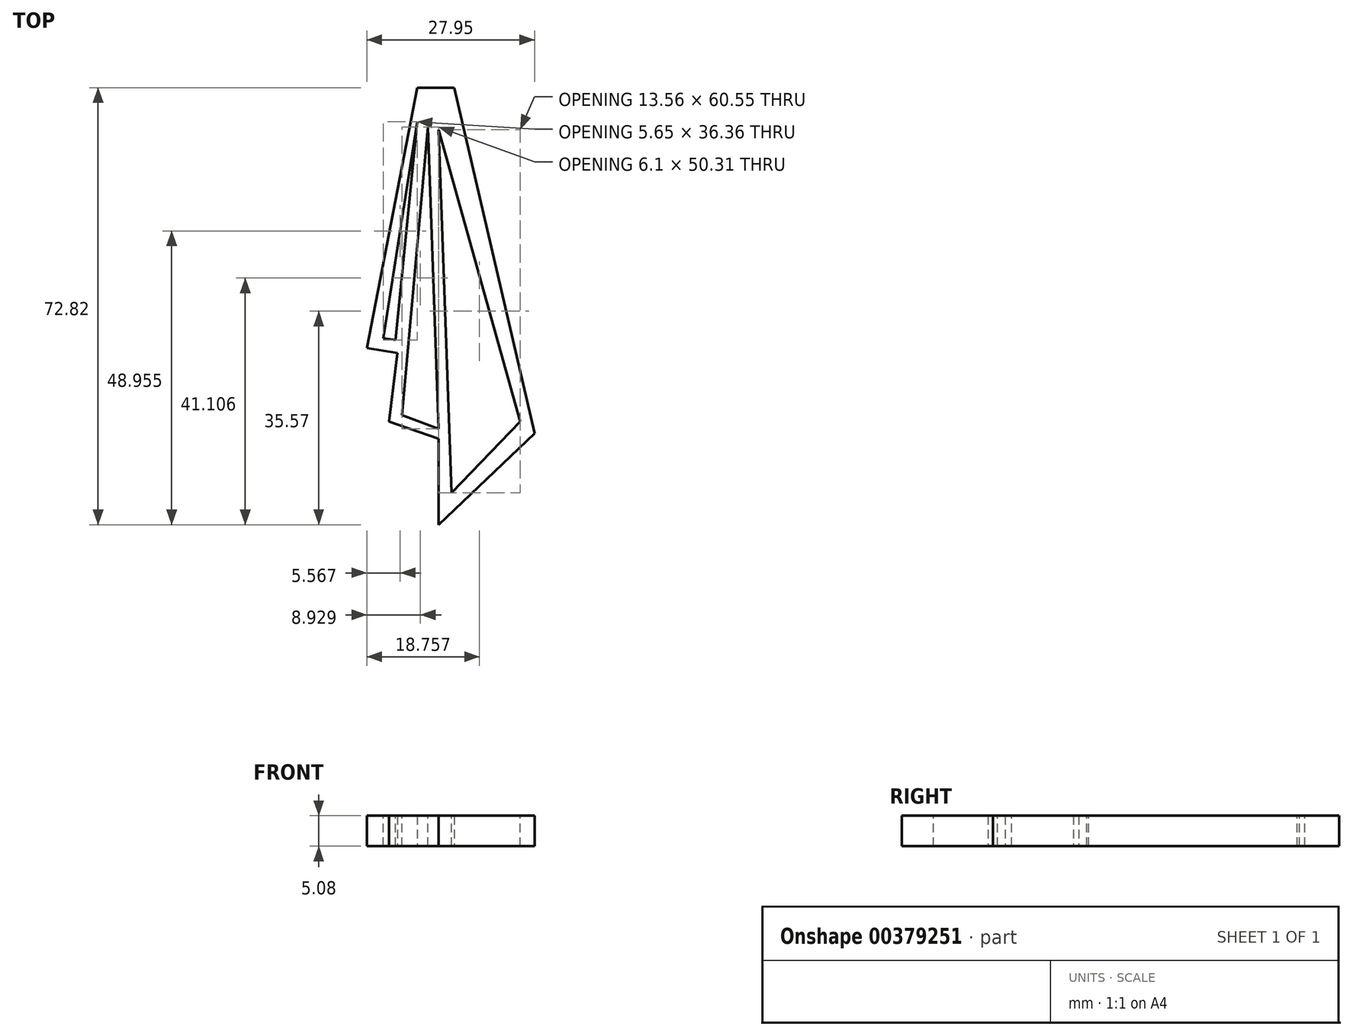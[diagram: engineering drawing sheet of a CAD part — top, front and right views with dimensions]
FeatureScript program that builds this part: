
annotation { "Feature Type Name" : "Feature", "Feature Type Description" : "" }
export const myFeature = defineFeature(function(context is Context, id is Id, definition is map)
    precondition{}
    {
        {
            var Q0;
            Q0=qCreatedBy(makeId("Top.planeOp"),FACE);
            var sketch = newSketch(context, id + "F0", { "sketchPlane" : qUnion([Q0])});
            skLineSegment(sketch, "E0", {"start": v(0, 0) * mm, "end": v(-8.4, -43.35) * mm});
            skLineSegment(sketch, "E1", {"start": v(-8.4, -43.35) * mm, "end": v(-3.26, -44.21) * mm});
            skLineSegment(sketch, "E2", {"start": v(-3.26, -44.21) * mm, "end": v(-4.68, -55.62) * mm});
            skLineSegment(sketch, "E3", {"start": v(-4.68, -55.62) * mm, "end": v(3.59, -58.47) * mm});
            skLineSegment(sketch, "E4", {"start": v(3.59, -58.47) * mm, "end": v(3.59, -72.82) * mm});
            skLineSegment(sketch, "E5", {"start": v(3.59, -72.82) * mm, "end": v(19.56, -57.61) * mm});
            skLineSegment(sketch, "E6", {"start": v(19.56, -57.61) * mm, "end": v(6.15, 0) * mm});
            skLineSegment(sketch, "E7", {"start": v(6.15, 0) * mm, "end": v(0, 0) * mm});
            skSolve(sketch);
        }
        {
            var Q0;
            Q0=makeQuery(id+"F0.imprint","IMPRINT",FACE,{"disambiguationData":[TD([[makeQuery(id+"F0.imprint","IMPRINT",EDGE,{"derivedFrom":sQuery(id+"F0.wireOp",EDGE,"E0")}),1.0]])]});
            extrude(context, id + "F1", {"entities" : qUnion([Q0]), "depth" : 5.08 * mm});
        }
        {
            var Q0;
            Q0=makeQuery(id+"F1.opExtrude","CAP_FACE",FACE,{"disambiguationData":[OSD([sQuery(id+"F0.wireOp",EDGE,"E0"),sQuery(id+"F0.wireOp",EDGE,"E1"),sQuery(id+"F0.wireOp",EDGE,"E2"),sQuery(id+"F0.wireOp",EDGE,"E3"),sQuery(id+"F0.wireOp",EDGE,"E4"),sQuery(id+"F0.wireOp",EDGE,"E5"),sQuery(id+"F0.wireOp",EDGE,"E6"),sQuery(id+"F0.wireOp",EDGE,"E7")])],"isStart":false});
            var sketch = newSketch(context, id + "F2", { "sketchPlane" : qUnion([Q0])});
            skLineSegment(sketch, "E8", {"start": v(0, -5.69) * mm, "end": v(-5.65, -41.72) * mm});
            skLineSegment(sketch, "E9", {"start": v(-5.65, -41.72) * mm, "end": v(-3.6, -42.04) * mm});
            skLineSegment(sketch, "E10", {"start": v(-3.6, -42.04) * mm, "end": v(0, -5.69) * mm});
            skLineSegment(sketch, "E11", {"start": v(-2.5, -54.53) * mm, "end": v(1.83, -6.56) * mm});
            skLineSegment(sketch, "E12", {"start": v(1.83, -6.56) * mm, "end": v(3.59, -56.87) * mm});
            skLineSegment(sketch, "E13", {"start": v(3.59, -56.87) * mm, "end": v(-2.5, -54.53) * mm});
            skLineSegment(sketch, "E14", {"start": v(3.59, -6.97) * mm, "end": v(5.7, -67.53) * mm});
            skLineSegment(sketch, "E15", {"start": v(5.7, -67.53) * mm, "end": v(17.15, -55.62) * mm});
            skLineSegment(sketch, "E16", {"start": v(17.15, -55.62) * mm, "end": v(3.59, -6.97) * mm});
            skSolve(sketch);
        }
        {
            var Q0;
            Q0 = qSketchRegion(id + "F2", true);
            extrude(context, id + "F3", {"entities" : qUnion([Q0]), "operationType" : NewBodyOperationType.REMOVE, "endBound" : BoundingType.THROUGH_ALL, "oppositeDirection" : true, "depth" : 25.4 * mm});
        }
    });
